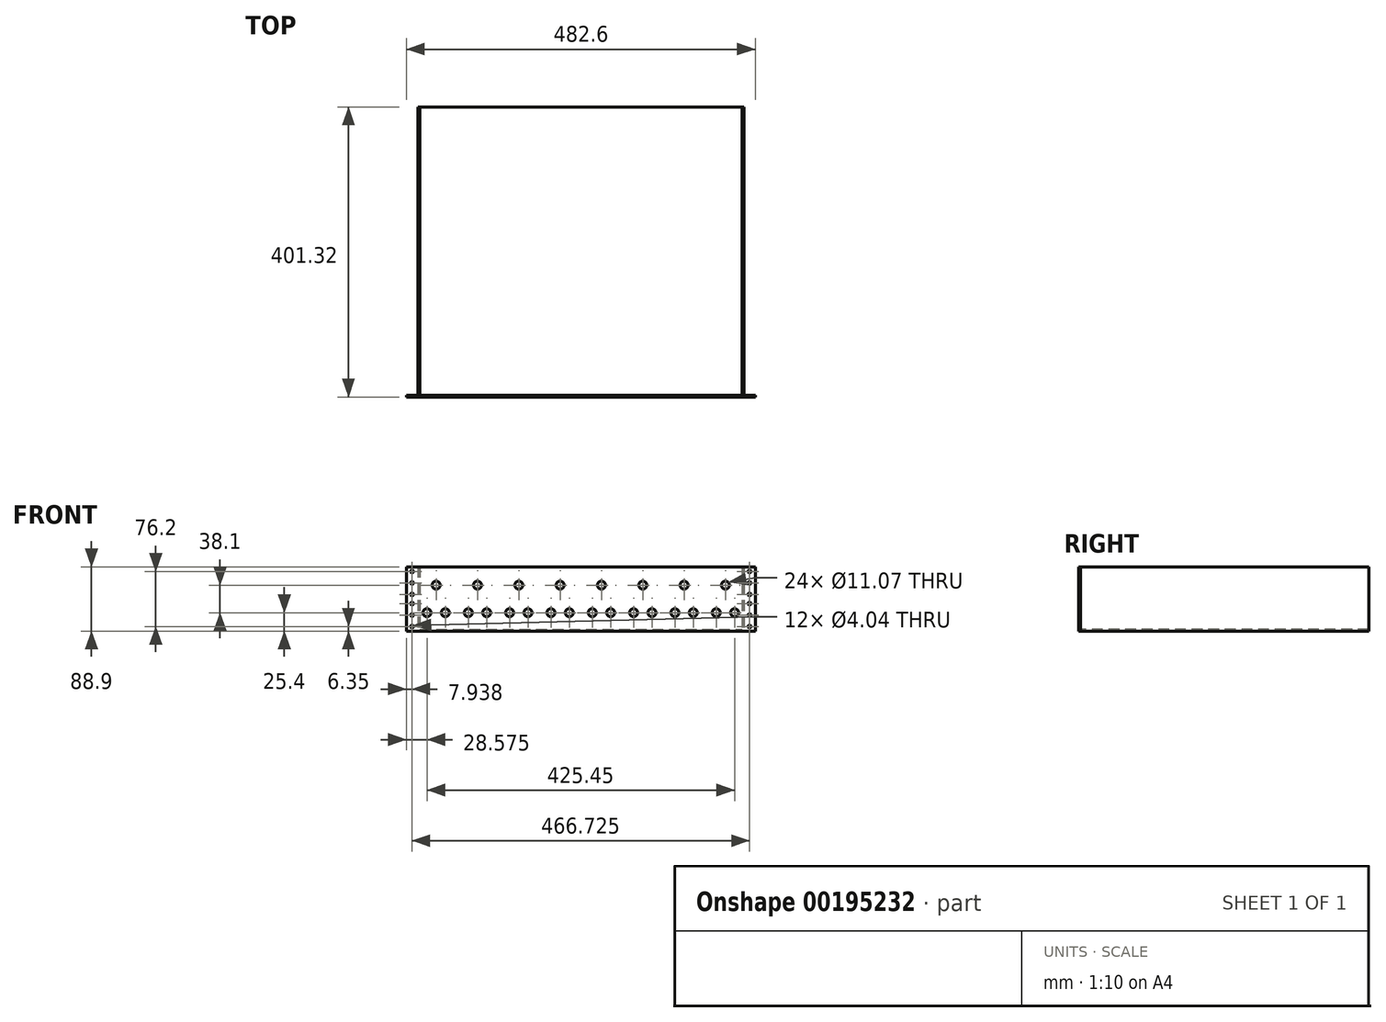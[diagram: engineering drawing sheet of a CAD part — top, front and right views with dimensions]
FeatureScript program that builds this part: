
annotation { "Feature Type Name" : "Feature", "Feature Type Description" : "" }
export const myFeature = defineFeature(function(context is Context, id is Id, definition is map)
    precondition{}
    {
        {
            var Q0;
            Q0=qCreatedBy(makeId("Front.planeOp"),FACE);
            var sketch = newSketch(context, id + "F0", { "sketchPlane" : qUnion([Q0])});
            skLineSegment(sketch, "E0.bottom", {"start": v(-241.3, 44.45) * mm, "end": v(241.3, 44.45) * mm});
            skLineSegment(sketch, "E0.top", {"start": v(-241.3, -44.45) * mm, "end": v(241.3, -44.45) * mm});
            skLineSegment(sketch, "E0.left", {"start": v(-241.3, 44.45) * mm, "end": v(-241.3, -44.45) * mm});
            skLineSegment(sketch, "E0.right", {"start": v(241.3, 44.45) * mm, "end": v(241.3, -44.45) * mm});
            skPoint(sketch, "E0.middle", {"position": v(0, 0) * mm});
            skCircle(sketch, "E1", {"center": v(-200.03, 19.05) * mm, "radius": 5.54 * mm});
            skCircle(sketch, "E2", {"center": v(-212.72, -19.05) * mm, "radius": 5.54 * mm});
            skCircle(sketch, "E3", {"center": v(-187.32, -19.05) * mm, "radius": 5.54 * mm});
            skCircle(sketch, "E4.1.0.0", {"center": v(-142.88, 19.05) * mm, "radius": 5.54 * mm});
            skCircle(sketch, "E4.1.0.1", {"center": v(-130.17, -19.05) * mm, "radius": 5.54 * mm});
            skCircle(sketch, "E4.1.0.2", {"center": v(-155.57, -19.05) * mm, "radius": 5.54 * mm});
            skCircle(sketch, "E4.2.0.0", {"center": v(-85.73, 19.05) * mm, "radius": 5.54 * mm});
            skCircle(sketch, "E4.2.0.1", {"center": v(-73.02, -19.05) * mm, "radius": 5.54 * mm});
            skCircle(sketch, "E4.2.0.2", {"center": v(-98.42, -19.05) * mm, "radius": 5.54 * mm});
            skCircle(sketch, "E4.3.0.0", {"center": v(-28.58, 19.05) * mm, "radius": 5.54 * mm});
            skCircle(sketch, "E4.3.0.1", {"center": v(-15.88, -19.05) * mm, "radius": 5.54 * mm});
            skCircle(sketch, "E4.3.0.2", {"center": v(-41.28, -19.05) * mm, "radius": 5.54 * mm});
            skCircle(sketch, "E4.4.0.0", {"center": v(28.57, 19.05) * mm, "radius": 5.54 * mm});
            skCircle(sketch, "E4.4.0.1", {"center": v(41.28, -19.05) * mm, "radius": 5.54 * mm});
            skCircle(sketch, "E4.4.0.2", {"center": v(15.88, -19.05) * mm, "radius": 5.54 * mm});
            skCircle(sketch, "E4.5.0.0", {"center": v(85.72, 19.05) * mm, "radius": 5.54 * mm});
            skCircle(sketch, "E4.5.0.1", {"center": v(98.43, -19.05) * mm, "radius": 5.54 * mm});
            skCircle(sketch, "E4.5.0.2", {"center": v(73.03, -19.05) * mm, "radius": 5.54 * mm});
            skCircle(sketch, "E4.6.0.0", {"center": v(142.87, 19.05) * mm, "radius": 5.54 * mm});
            skCircle(sketch, "E4.6.0.1", {"center": v(155.57, -19.05) * mm, "radius": 5.54 * mm});
            skCircle(sketch, "E4.6.0.2", {"center": v(130.17, -19.05) * mm, "radius": 5.54 * mm});
            skCircle(sketch, "E4.7.0.0", {"center": v(200.03, 19.05) * mm, "radius": 5.54 * mm});
            skCircle(sketch, "E4.7.0.1", {"center": v(212.73, -19.05) * mm, "radius": 5.54 * mm});
            skCircle(sketch, "E4.7.0.2", {"center": v(187.33, -19.05) * mm, "radius": 5.54 * mm});
            skLineSegment(sketch, "E4.direction1", {"start": v(-200.03, 19.05) * mm, "end": v(-142.88, 19.05) * mm, "construction": true});
            skSolve(sketch);
        }
        {
            var Q0;
            Q0=makeQuery(id+"F0.imprint","IMPRINT",FACE,{"disambiguationData":[TD([[makeQuery(id+"F0.imprint","IMPRINT",EDGE,{"derivedFrom":sQuery(id+"F0.wireOp",EDGE,"E0.bottom")}),-1.0]])]});
            extrude(context, id + "F1", {"entities" : qUnion([Q0]), "depth" : 2.54 * mm});
        }
        {
            var Q0;
            Q0=makeQuery(id+"F1.opExtrude","CAP_FACE",FACE,{"disambiguationData":[OSD([sQuery(id+"F0.wireOp",EDGE,"E0.bottom"),sQuery(id+"F0.wireOp",EDGE,"E0.top"),sQuery(id+"F0.wireOp",EDGE,"E0.left"),sQuery(id+"F0.wireOp",EDGE,"E0.right"),sQuery(id+"F0.wireOp",EDGE,"E1"),sQuery(id+"F0.wireOp",EDGE,"E2"),sQuery(id+"F0.wireOp",EDGE,"E3"),sQuery(id+"F0.wireOp",EDGE,"E4.1.0.0"),sQuery(id+"F0.wireOp",EDGE,"E4.1.0.1"),sQuery(id+"F0.wireOp",EDGE,"E4.1.0.2"),sQuery(id+"F0.wireOp",EDGE,"E4.2.0.0"),sQuery(id+"F0.wireOp",EDGE,"E4.2.0.1"),sQuery(id+"F0.wireOp",EDGE,"E4.2.0.2"),sQuery(id+"F0.wireOp",EDGE,"E4.3.0.0"),sQuery(id+"F0.wireOp",EDGE,"E4.3.0.1"),sQuery(id+"F0.wireOp",EDGE,"E4.3.0.2"),sQuery(id+"F0.wireOp",EDGE,"E4.4.0.0"),sQuery(id+"F0.wireOp",EDGE,"E4.4.0.1"),sQuery(id+"F0.wireOp",EDGE,"E4.4.0.2"),sQuery(id+"F0.wireOp",EDGE,"E4.5.0.0"),sQuery(id+"F0.wireOp",EDGE,"E4.5.0.1"),sQuery(id+"F0.wireOp",EDGE,"E4.5.0.2"),sQuery(id+"F0.wireOp",EDGE,"E4.6.0.0"),sQuery(id+"F0.wireOp",EDGE,"E4.6.0.1"),sQuery(id+"F0.wireOp",EDGE,"E4.6.0.2"),sQuery(id+"F0.wireOp",EDGE,"E4.7.0.0"),sQuery(id+"F0.wireOp",EDGE,"E4.7.0.1"),sQuery(id+"F0.wireOp",EDGE,"E4.7.0.2")])],"isStart":true});
            var sketch = newSketch(context, id + "F2", { "sketchPlane" : qUnion([Q0])});
            skLineSegment(sketch, "E5.bottom", {"start": v(-225.43, 44.45) * mm, "end": v(225.43, 44.45) * mm});
            skLineSegment(sketch, "E5.top", {"start": v(-225.43, -44.45) * mm, "end": v(225.43, -44.45) * mm});
            skLineSegment(sketch, "E5.left", {"start": v(-225.43, 44.45) * mm, "end": v(-225.43, -44.45) * mm});
            skLineSegment(sketch, "E5.right", {"start": v(225.43, 44.45) * mm, "end": v(225.43, -44.45) * mm});
            skPoint(sketch, "E5.middle", {"position": v(0, 0) * mm});
            skSolve(sketch);
        }
        {
            var Q0;
            Q0 = qSketchRegion(id + "F2", true);
            var Q1;
            Q1=sQuery(id+"F2.wireOp",EDGE,"E5.left");
            var Q2;
            Q2=sQuery(id+"F2.wireOp",EDGE,"E5.bottom");
            var Q3;
            Q3=sQuery(id+"F2.wireOp",EDGE,"E5.top");
            var Q4;
            Q4=sQuery(id+"F2.wireOp",EDGE,"E5.right");
            extrude(context, id + "F3", {"entities" : qUnion([Q0]), "operationType" : NewBodyOperationType.ADD, "surfaceEntities" : qUnion([Q1, Q2, Q3, Q4]), "depth" : 398.78 * mm});
        }
        {
            var Q0;
            Q0=makeQuery(id+"F3.boolean.opBoolean","SPLIT",FACE,{"disambiguationData":[TD([makeQuery(id+"F1.opExtrude","SWEPT_FACE",FACE,{"disambiguationData":[OSD([sQuery(id+"F0.wireOp",EDGE,"E1")])]})])],"derivedFrom":makeQuery(id+"F3.opExtrude","CAP_FACE",FACE,{"disambiguationData":[OSD([sQuery(id+"F2.wireOp",EDGE,"E5.bottom"),sQuery(id+"F2.wireOp",EDGE,"E5.top"),sQuery(id+"F2.wireOp",EDGE,"E5.left"),sQuery(id+"F2.wireOp",EDGE,"E5.right")])],"isStart":true})});
            var Q1;
            Q1=makeQuery(id+"F3.boolean.opBoolean","SPLIT",FACE,{"disambiguationData":[TD([makeQuery(id+"F1.opExtrude","SWEPT_FACE",FACE,{"disambiguationData":[OSD([sQuery(id+"F0.wireOp",EDGE,"E2")])]})])],"derivedFrom":makeQuery(id+"F3.opExtrude","CAP_FACE",FACE,{"disambiguationData":[OSD([sQuery(id+"F2.wireOp",EDGE,"E5.bottom"),sQuery(id+"F2.wireOp",EDGE,"E5.top"),sQuery(id+"F2.wireOp",EDGE,"E5.left"),sQuery(id+"F2.wireOp",EDGE,"E5.right")])],"isStart":true})});
            var Q2;
            Q2=makeQuery(id+"F3.boolean.opBoolean","SPLIT",FACE,{"disambiguationData":[TD([makeQuery(id+"F1.opExtrude","SWEPT_FACE",FACE,{"disambiguationData":[OSD([sQuery(id+"F0.wireOp",EDGE,"E3")])]})])],"derivedFrom":makeQuery(id+"F3.opExtrude","CAP_FACE",FACE,{"disambiguationData":[OSD([sQuery(id+"F2.wireOp",EDGE,"E5.bottom"),sQuery(id+"F2.wireOp",EDGE,"E5.top"),sQuery(id+"F2.wireOp",EDGE,"E5.left"),sQuery(id+"F2.wireOp",EDGE,"E5.right")])],"isStart":true})});
            var Q3;
            Q3=makeQuery(id+"F3.boolean.opBoolean","SPLIT",FACE,{"disambiguationData":[TD([makeQuery(id+"F1.opExtrude","SWEPT_FACE",FACE,{"disambiguationData":[OSD([sQuery(id+"F0.wireOp",EDGE,"E4.1.0.0")])]})])],"derivedFrom":makeQuery(id+"F3.opExtrude","CAP_FACE",FACE,{"disambiguationData":[OSD([sQuery(id+"F2.wireOp",EDGE,"E5.bottom"),sQuery(id+"F2.wireOp",EDGE,"E5.top"),sQuery(id+"F2.wireOp",EDGE,"E5.left"),sQuery(id+"F2.wireOp",EDGE,"E5.right")])],"isStart":true})});
            var Q4;
            Q4=makeQuery(id+"F3.boolean.opBoolean","SPLIT",FACE,{"disambiguationData":[TD([makeQuery(id+"F1.opExtrude","SWEPT_FACE",FACE,{"disambiguationData":[OSD([sQuery(id+"F0.wireOp",EDGE,"E4.1.0.2")])]})])],"derivedFrom":makeQuery(id+"F3.opExtrude","CAP_FACE",FACE,{"disambiguationData":[OSD([sQuery(id+"F2.wireOp",EDGE,"E5.bottom"),sQuery(id+"F2.wireOp",EDGE,"E5.top"),sQuery(id+"F2.wireOp",EDGE,"E5.left"),sQuery(id+"F2.wireOp",EDGE,"E5.right")])],"isStart":true})});
            var Q5;
            Q5=makeQuery(id+"F3.boolean.opBoolean","SPLIT",FACE,{"disambiguationData":[TD([makeQuery(id+"F1.opExtrude","SWEPT_FACE",FACE,{"disambiguationData":[OSD([sQuery(id+"F0.wireOp",EDGE,"E4.1.0.1")])]})])],"derivedFrom":makeQuery(id+"F3.opExtrude","CAP_FACE",FACE,{"disambiguationData":[OSD([sQuery(id+"F2.wireOp",EDGE,"E5.bottom"),sQuery(id+"F2.wireOp",EDGE,"E5.top"),sQuery(id+"F2.wireOp",EDGE,"E5.left"),sQuery(id+"F2.wireOp",EDGE,"E5.right")])],"isStart":true})});
            var Q6;
            Q6=makeQuery(id+"F3.boolean.opBoolean","SPLIT",FACE,{"disambiguationData":[TD([makeQuery(id+"F1.opExtrude","SWEPT_FACE",FACE,{"disambiguationData":[OSD([sQuery(id+"F0.wireOp",EDGE,"E4.2.0.0")])]})])],"derivedFrom":makeQuery(id+"F3.opExtrude","CAP_FACE",FACE,{"disambiguationData":[OSD([sQuery(id+"F2.wireOp",EDGE,"E5.bottom"),sQuery(id+"F2.wireOp",EDGE,"E5.top"),sQuery(id+"F2.wireOp",EDGE,"E5.left"),sQuery(id+"F2.wireOp",EDGE,"E5.right")])],"isStart":true})});
            var Q7;
            Q7=makeQuery(id+"F3.boolean.opBoolean","SPLIT",FACE,{"disambiguationData":[TD([makeQuery(id+"F1.opExtrude","SWEPT_FACE",FACE,{"disambiguationData":[OSD([sQuery(id+"F0.wireOp",EDGE,"E4.2.0.2")])]})])],"derivedFrom":makeQuery(id+"F3.opExtrude","CAP_FACE",FACE,{"disambiguationData":[OSD([sQuery(id+"F2.wireOp",EDGE,"E5.bottom"),sQuery(id+"F2.wireOp",EDGE,"E5.top"),sQuery(id+"F2.wireOp",EDGE,"E5.left"),sQuery(id+"F2.wireOp",EDGE,"E5.right")])],"isStart":true})});
            var Q8;
            Q8=makeQuery(id+"F3.boolean.opBoolean","SPLIT",FACE,{"disambiguationData":[TD([makeQuery(id+"F1.opExtrude","SWEPT_FACE",FACE,{"disambiguationData":[OSD([sQuery(id+"F0.wireOp",EDGE,"E4.2.0.1")])]})])],"derivedFrom":makeQuery(id+"F3.opExtrude","CAP_FACE",FACE,{"disambiguationData":[OSD([sQuery(id+"F2.wireOp",EDGE,"E5.bottom"),sQuery(id+"F2.wireOp",EDGE,"E5.top"),sQuery(id+"F2.wireOp",EDGE,"E5.left"),sQuery(id+"F2.wireOp",EDGE,"E5.right")])],"isStart":true})});
            var Q9;
            Q9=makeQuery(id+"F3.boolean.opBoolean","SPLIT",FACE,{"disambiguationData":[TD([makeQuery(id+"F1.opExtrude","SWEPT_FACE",FACE,{"disambiguationData":[OSD([sQuery(id+"F0.wireOp",EDGE,"E4.3.0.2")])]})])],"derivedFrom":makeQuery(id+"F3.opExtrude","CAP_FACE",FACE,{"disambiguationData":[OSD([sQuery(id+"F2.wireOp",EDGE,"E5.bottom"),sQuery(id+"F2.wireOp",EDGE,"E5.top"),sQuery(id+"F2.wireOp",EDGE,"E5.left"),sQuery(id+"F2.wireOp",EDGE,"E5.right")])],"isStart":true})});
            var Q10;
            Q10=makeQuery(id+"F3.boolean.opBoolean","SPLIT",FACE,{"disambiguationData":[TD([makeQuery(id+"F1.opExtrude","SWEPT_FACE",FACE,{"disambiguationData":[OSD([sQuery(id+"F0.wireOp",EDGE,"E4.3.0.0")])]})])],"derivedFrom":makeQuery(id+"F3.opExtrude","CAP_FACE",FACE,{"disambiguationData":[OSD([sQuery(id+"F2.wireOp",EDGE,"E5.bottom"),sQuery(id+"F2.wireOp",EDGE,"E5.top"),sQuery(id+"F2.wireOp",EDGE,"E5.left"),sQuery(id+"F2.wireOp",EDGE,"E5.right")])],"isStart":true})});
            var Q11;
            Q11=makeQuery(id+"F3.boolean.opBoolean","SPLIT",FACE,{"disambiguationData":[TD([makeQuery(id+"F1.opExtrude","SWEPT_FACE",FACE,{"disambiguationData":[OSD([sQuery(id+"F0.wireOp",EDGE,"E4.3.0.1")])]})])],"derivedFrom":makeQuery(id+"F3.opExtrude","CAP_FACE",FACE,{"disambiguationData":[OSD([sQuery(id+"F2.wireOp",EDGE,"E5.bottom"),sQuery(id+"F2.wireOp",EDGE,"E5.top"),sQuery(id+"F2.wireOp",EDGE,"E5.left"),sQuery(id+"F2.wireOp",EDGE,"E5.right")])],"isStart":true})});
            var Q12;
            Q12=makeQuery(id+"F3.boolean.opBoolean","SPLIT",FACE,{"disambiguationData":[TD([makeQuery(id+"F1.opExtrude","SWEPT_FACE",FACE,{"disambiguationData":[OSD([sQuery(id+"F0.wireOp",EDGE,"E4.4.0.2")])]})])],"derivedFrom":makeQuery(id+"F3.opExtrude","CAP_FACE",FACE,{"disambiguationData":[OSD([sQuery(id+"F2.wireOp",EDGE,"E5.bottom"),sQuery(id+"F2.wireOp",EDGE,"E5.top"),sQuery(id+"F2.wireOp",EDGE,"E5.left"),sQuery(id+"F2.wireOp",EDGE,"E5.right")])],"isStart":true})});
            var Q13;
            Q13=makeQuery(id+"F3.boolean.opBoolean","SPLIT",FACE,{"disambiguationData":[TD([makeQuery(id+"F1.opExtrude","SWEPT_FACE",FACE,{"disambiguationData":[OSD([sQuery(id+"F0.wireOp",EDGE,"E4.4.0.0")])]})])],"derivedFrom":makeQuery(id+"F3.opExtrude","CAP_FACE",FACE,{"disambiguationData":[OSD([sQuery(id+"F2.wireOp",EDGE,"E5.bottom"),sQuery(id+"F2.wireOp",EDGE,"E5.top"),sQuery(id+"F2.wireOp",EDGE,"E5.left"),sQuery(id+"F2.wireOp",EDGE,"E5.right")])],"isStart":true})});
            var Q14;
            Q14=makeQuery(id+"F3.boolean.opBoolean","SPLIT",FACE,{"disambiguationData":[TD([makeQuery(id+"F1.opExtrude","SWEPT_FACE",FACE,{"disambiguationData":[OSD([sQuery(id+"F0.wireOp",EDGE,"E4.4.0.1")])]})])],"derivedFrom":makeQuery(id+"F3.opExtrude","CAP_FACE",FACE,{"disambiguationData":[OSD([sQuery(id+"F2.wireOp",EDGE,"E5.bottom"),sQuery(id+"F2.wireOp",EDGE,"E5.top"),sQuery(id+"F2.wireOp",EDGE,"E5.left"),sQuery(id+"F2.wireOp",EDGE,"E5.right")])],"isStart":true})});
            var Q15;
            Q15=makeQuery(id+"F3.boolean.opBoolean","SPLIT",FACE,{"disambiguationData":[TD([makeQuery(id+"F1.opExtrude","SWEPT_FACE",FACE,{"disambiguationData":[OSD([sQuery(id+"F0.wireOp",EDGE,"E4.5.0.2")])]})])],"derivedFrom":makeQuery(id+"F3.opExtrude","CAP_FACE",FACE,{"disambiguationData":[OSD([sQuery(id+"F2.wireOp",EDGE,"E5.bottom"),sQuery(id+"F2.wireOp",EDGE,"E5.top"),sQuery(id+"F2.wireOp",EDGE,"E5.left"),sQuery(id+"F2.wireOp",EDGE,"E5.right")])],"isStart":true})});
            var Q16;
            Q16=makeQuery(id+"F3.boolean.opBoolean","SPLIT",FACE,{"disambiguationData":[TD([makeQuery(id+"F1.opExtrude","SWEPT_FACE",FACE,{"disambiguationData":[OSD([sQuery(id+"F0.wireOp",EDGE,"E4.5.0.0")])]})])],"derivedFrom":makeQuery(id+"F3.opExtrude","CAP_FACE",FACE,{"disambiguationData":[OSD([sQuery(id+"F2.wireOp",EDGE,"E5.bottom"),sQuery(id+"F2.wireOp",EDGE,"E5.top"),sQuery(id+"F2.wireOp",EDGE,"E5.left"),sQuery(id+"F2.wireOp",EDGE,"E5.right")])],"isStart":true})});
            var Q17;
            Q17=makeQuery(id+"F3.boolean.opBoolean","SPLIT",FACE,{"disambiguationData":[TD([makeQuery(id+"F1.opExtrude","SWEPT_FACE",FACE,{"disambiguationData":[OSD([sQuery(id+"F0.wireOp",EDGE,"E4.5.0.1")])]})])],"derivedFrom":makeQuery(id+"F3.opExtrude","CAP_FACE",FACE,{"disambiguationData":[OSD([sQuery(id+"F2.wireOp",EDGE,"E5.bottom"),sQuery(id+"F2.wireOp",EDGE,"E5.top"),sQuery(id+"F2.wireOp",EDGE,"E5.left"),sQuery(id+"F2.wireOp",EDGE,"E5.right")])],"isStart":true})});
            var Q18;
            Q18=makeQuery(id+"F3.boolean.opBoolean","SPLIT",FACE,{"disambiguationData":[TD([makeQuery(id+"F1.opExtrude","SWEPT_FACE",FACE,{"disambiguationData":[OSD([sQuery(id+"F0.wireOp",EDGE,"E4.6.0.2")])]})])],"derivedFrom":makeQuery(id+"F3.opExtrude","CAP_FACE",FACE,{"disambiguationData":[OSD([sQuery(id+"F2.wireOp",EDGE,"E5.bottom"),sQuery(id+"F2.wireOp",EDGE,"E5.top"),sQuery(id+"F2.wireOp",EDGE,"E5.left"),sQuery(id+"F2.wireOp",EDGE,"E5.right")])],"isStart":true})});
            var Q19;
            Q19=makeQuery(id+"F3.boolean.opBoolean","SPLIT",FACE,{"disambiguationData":[TD([makeQuery(id+"F1.opExtrude","SWEPT_FACE",FACE,{"disambiguationData":[OSD([sQuery(id+"F0.wireOp",EDGE,"E4.6.0.0")])]})])],"derivedFrom":makeQuery(id+"F3.opExtrude","CAP_FACE",FACE,{"disambiguationData":[OSD([sQuery(id+"F2.wireOp",EDGE,"E5.bottom"),sQuery(id+"F2.wireOp",EDGE,"E5.top"),sQuery(id+"F2.wireOp",EDGE,"E5.left"),sQuery(id+"F2.wireOp",EDGE,"E5.right")])],"isStart":true})});
            var Q20;
            Q20=makeQuery(id+"F3.boolean.opBoolean","SPLIT",FACE,{"disambiguationData":[TD([makeQuery(id+"F1.opExtrude","SWEPT_FACE",FACE,{"disambiguationData":[OSD([sQuery(id+"F0.wireOp",EDGE,"E4.6.0.1")])]})])],"derivedFrom":makeQuery(id+"F3.opExtrude","CAP_FACE",FACE,{"disambiguationData":[OSD([sQuery(id+"F2.wireOp",EDGE,"E5.bottom"),sQuery(id+"F2.wireOp",EDGE,"E5.top"),sQuery(id+"F2.wireOp",EDGE,"E5.left"),sQuery(id+"F2.wireOp",EDGE,"E5.right")])],"isStart":true})});
            var Q21;
            Q21=makeQuery(id+"F3.boolean.opBoolean","SPLIT",FACE,{"disambiguationData":[TD([makeQuery(id+"F1.opExtrude","SWEPT_FACE",FACE,{"disambiguationData":[OSD([sQuery(id+"F0.wireOp",EDGE,"E4.7.0.2")])]})])],"derivedFrom":makeQuery(id+"F3.opExtrude","CAP_FACE",FACE,{"disambiguationData":[OSD([sQuery(id+"F2.wireOp",EDGE,"E5.bottom"),sQuery(id+"F2.wireOp",EDGE,"E5.top"),sQuery(id+"F2.wireOp",EDGE,"E5.left"),sQuery(id+"F2.wireOp",EDGE,"E5.right")])],"isStart":true})});
            var Q22;
            Q22=makeQuery(id+"F3.boolean.opBoolean","SPLIT",FACE,{"disambiguationData":[TD([makeQuery(id+"F1.opExtrude","SWEPT_FACE",FACE,{"disambiguationData":[OSD([sQuery(id+"F0.wireOp",EDGE,"E4.7.0.0")])]})])],"derivedFrom":makeQuery(id+"F3.opExtrude","CAP_FACE",FACE,{"disambiguationData":[OSD([sQuery(id+"F2.wireOp",EDGE,"E5.bottom"),sQuery(id+"F2.wireOp",EDGE,"E5.top"),sQuery(id+"F2.wireOp",EDGE,"E5.left"),sQuery(id+"F2.wireOp",EDGE,"E5.right")])],"isStart":true})});
            var Q23;
            Q23=makeQuery(id+"F3.boolean.opBoolean","SPLIT",FACE,{"disambiguationData":[TD([makeQuery(id+"F1.opExtrude","SWEPT_FACE",FACE,{"disambiguationData":[OSD([sQuery(id+"F0.wireOp",EDGE,"E4.7.0.1")])]})])],"derivedFrom":makeQuery(id+"F3.opExtrude","CAP_FACE",FACE,{"disambiguationData":[OSD([sQuery(id+"F2.wireOp",EDGE,"E5.bottom"),sQuery(id+"F2.wireOp",EDGE,"E5.top"),sQuery(id+"F2.wireOp",EDGE,"E5.left"),sQuery(id+"F2.wireOp",EDGE,"E5.right")])],"isStart":true})});
            extrude(context, id + "F4", {"entities" : qUnion([Q0, Q1, Q2, Q3, Q4, Q5, Q6, Q7, Q8, Q9, Q10, Q11, Q12, Q13, Q14, Q15, Q16, Q17, Q18, Q19, Q20, Q21, Q22, Q23]), "operationType" : NewBodyOperationType.REMOVE, "endBound" : BoundingType.THROUGH_ALL, "oppositeDirection" : true, "depth" : 25.4 * mm});
        }
        {
            var Q0;
            Q0=makeQuery(id+"F1.opExtrude","CAP_FACE",FACE,{"disambiguationData":[OSD([sQuery(id+"F0.wireOp",EDGE,"E0.bottom"),sQuery(id+"F0.wireOp",EDGE,"E0.top"),sQuery(id+"F0.wireOp",EDGE,"E0.left"),sQuery(id+"F0.wireOp",EDGE,"E0.right"),sQuery(id+"F0.wireOp",EDGE,"E1"),sQuery(id+"F0.wireOp",EDGE,"E2"),sQuery(id+"F0.wireOp",EDGE,"E3"),sQuery(id+"F0.wireOp",EDGE,"E4.1.0.0"),sQuery(id+"F0.wireOp",EDGE,"E4.1.0.1"),sQuery(id+"F0.wireOp",EDGE,"E4.1.0.2"),sQuery(id+"F0.wireOp",EDGE,"E4.2.0.0"),sQuery(id+"F0.wireOp",EDGE,"E4.2.0.1"),sQuery(id+"F0.wireOp",EDGE,"E4.2.0.2"),sQuery(id+"F0.wireOp",EDGE,"E4.3.0.0"),sQuery(id+"F0.wireOp",EDGE,"E4.3.0.1"),sQuery(id+"F0.wireOp",EDGE,"E4.3.0.2"),sQuery(id+"F0.wireOp",EDGE,"E4.4.0.0"),sQuery(id+"F0.wireOp",EDGE,"E4.4.0.1"),sQuery(id+"F0.wireOp",EDGE,"E4.4.0.2"),sQuery(id+"F0.wireOp",EDGE,"E4.5.0.0"),sQuery(id+"F0.wireOp",EDGE,"E4.5.0.1"),sQuery(id+"F0.wireOp",EDGE,"E4.5.0.2"),sQuery(id+"F0.wireOp",EDGE,"E4.6.0.0"),sQuery(id+"F0.wireOp",EDGE,"E4.6.0.1"),sQuery(id+"F0.wireOp",EDGE,"E4.6.0.2"),sQuery(id+"F0.wireOp",EDGE,"E4.7.0.0"),sQuery(id+"F0.wireOp",EDGE,"E4.7.0.1"),sQuery(id+"F0.wireOp",EDGE,"E4.7.0.2")])],"isStart":false});
            var sketch = newSketch(context, id + "F5", { "sketchPlane" : qUnion([Q0])});
            skPoint(sketch, "E6", {"position": v(-233.36, 38.1) * mm});
            skPoint(sketch, "E7", {"position": v(-233.36, 22.22) * mm});
            skPoint(sketch, "E8", {"position": v(-233.36, 6.35) * mm});
            skPoint(sketch, "E9.0.1.0", {"position": v(-233.36, -6.35) * mm});
            skPoint(sketch, "E9.0.1.1", {"position": v(-233.36, -22.23) * mm});
            skPoint(sketch, "E9.0.1.2", {"position": v(-233.36, -38.1) * mm});
            skPoint(sketch, "E9.1.0.0", {"position": v(233.36, 38.1) * mm});
            skPoint(sketch, "E9.1.0.1", {"position": v(233.36, 22.22) * mm});
            skPoint(sketch, "E9.1.0.2", {"position": v(233.36, 6.35) * mm});
            skPoint(sketch, "E9.1.1.0", {"position": v(233.36, -6.35) * mm});
            skPoint(sketch, "E9.1.1.1", {"position": v(233.36, -22.23) * mm});
            skPoint(sketch, "E9.1.1.2", {"position": v(233.36, -38.1) * mm});
            skLineSegment(sketch, "E9.direction1", {"start": v(-233.36, 38.1) * mm, "end": v(233.36, 38.1) * mm, "construction": true});
            skLineSegment(sketch, "E9.direction2", {"start": v(-233.36, 38.1) * mm, "end": v(-233.36, -6.35) * mm, "construction": true});
            skSolve(sketch);
        }
        {
            var Q0;
            Q0=sQuery(id+"F5.wireOp",VERTEX,"E9.1.1.2");
            var Q1;
            Q1=sQuery(id+"F5.wireOp",VERTEX,"E9.1.1.0");
            var Q2;
            Q2=sQuery(id+"F5.wireOp",VERTEX,"E7");
            var Q3;
            Q3=sQuery(id+"F5.wireOp",VERTEX,"E9.1.1.1");
            var Q4;
            Q4=sQuery(id+"F5.wireOp",VERTEX,"E6");
            var Q5;
            Q5=sQuery(id+"F5.wireOp",VERTEX,"E8");
            var Q6;
            Q6=sQuery(id+"F5.wireOp",VERTEX,"E9.0.1.1");
            var Q7;
            Q7=sQuery(id+"F5.wireOp",VERTEX,"E9.0.1.0");
            var Q8;
            Q8=sQuery(id+"F5.wireOp",VERTEX,"E9.0.1.2");
            var Q9;
            Q9=sQuery(id+"F5.wireOp",VERTEX,"E9.1.0.0");
            var Q10;
            Q10=sQuery(id+"F5.wireOp",VERTEX,"E9.1.0.1");
            var Q11;
            Q11=sQuery(id+"F5.wireOp",VERTEX,"E9.1.0.2");
            var Q12;
            Q12=makeQuery(id+"F1.opExtrude","SWEPT_BODY",BODY,{"disambiguationData":[OSD([sQuery(id+"F0.wireOp",EDGE,"E0.bottom"),sQuery(id+"F0.wireOp",EDGE,"E0.top"),sQuery(id+"F0.wireOp",EDGE,"E0.left"),sQuery(id+"F0.wireOp",EDGE,"E0.right"),sQuery(id+"F0.wireOp",EDGE,"E1"),sQuery(id+"F0.wireOp",EDGE,"E2"),sQuery(id+"F0.wireOp",EDGE,"E3"),sQuery(id+"F0.wireOp",EDGE,"E4.1.0.0"),sQuery(id+"F0.wireOp",EDGE,"E4.1.0.1"),sQuery(id+"F0.wireOp",EDGE,"E4.1.0.2"),sQuery(id+"F0.wireOp",EDGE,"E4.2.0.0"),sQuery(id+"F0.wireOp",EDGE,"E4.2.0.1"),sQuery(id+"F0.wireOp",EDGE,"E4.2.0.2"),sQuery(id+"F0.wireOp",EDGE,"E4.3.0.0"),sQuery(id+"F0.wireOp",EDGE,"E4.3.0.1"),sQuery(id+"F0.wireOp",EDGE,"E4.3.0.2"),sQuery(id+"F0.wireOp",EDGE,"E4.4.0.0"),sQuery(id+"F0.wireOp",EDGE,"E4.4.0.1"),sQuery(id+"F0.wireOp",EDGE,"E4.4.0.2"),sQuery(id+"F0.wireOp",EDGE,"E4.5.0.0"),sQuery(id+"F0.wireOp",EDGE,"E4.5.0.1"),sQuery(id+"F0.wireOp",EDGE,"E4.5.0.2"),sQuery(id+"F0.wireOp",EDGE,"E4.6.0.0"),sQuery(id+"F0.wireOp",EDGE,"E4.6.0.1"),sQuery(id+"F0.wireOp",EDGE,"E4.6.0.2"),sQuery(id+"F0.wireOp",EDGE,"E4.7.0.0"),sQuery(id+"F0.wireOp",EDGE,"E4.7.0.1"),sQuery(id+"F0.wireOp",EDGE,"E4.7.0.2")])]});
            hole(context, id + "F6", {"style" : HoleStyle.SIMPLE, "endStyle" : HoleEndStyle.THROUGH, "standardTappedOrClearance" : lookupTablePath({ "standard" : "ANSI", "engagement" : "75%", "pitch" : "32 tpi", "size" : "#10", "type" : "Tapped" }), "standardBlindInLast" : lookupTablePath({ "standard" : "ANSI", "engagement" : "75%", "pitch" : "32 tpi", "size" : "#10", "type" : "Tapped" }), "holeDiameter" : 4.04 * mm, "locations" : qUnion([Q0, Q1, Q2, Q3, Q4, Q5, Q6, Q7, Q8, Q9, Q10, Q11]), "scope" : qUnion([Q12]), "isTappedThrough" : true, "majorDiameter" : 4.83 * mm, "showTappedDepth" : true});
        }
        {
            var Q0;
            {var subQ0=sQuery(id+"F0.wireOp",EDGE,"E4.4.0.0");Q0=makeQuery(id+"F4.boolean.opBoolean","MERGE",FACE,{"derivedFrom":[makeQuery(id+"F1.opExtrude","SWEPT_FACE",FACE,{"disambiguationData":[OSD([subQ0])]}),makeQuery(id+"F4.opExtrude","SWEPT_FACE",FACE,{"disambiguationData":[OSD([subQ0])]})]});}
            var Q1;
            {var subQ0=sQuery(id+"F0.wireOp",EDGE,"E4.2.0.2");Q1=makeQuery(id+"F4.boolean.opBoolean","MERGE",FACE,{"derivedFrom":[makeQuery(id+"F1.opExtrude","SWEPT_FACE",FACE,{"disambiguationData":[OSD([subQ0])]}),makeQuery(id+"F4.opExtrude","SWEPT_FACE",FACE,{"disambiguationData":[OSD([subQ0])]})]});}
            var Q2;
            {var subQ0=sQuery(id+"F0.wireOp",EDGE,"E4.1.0.1");Q2=makeQuery(id+"F4.boolean.opBoolean","MERGE",FACE,{"derivedFrom":[makeQuery(id+"F1.opExtrude","SWEPT_FACE",FACE,{"disambiguationData":[OSD([subQ0])]}),makeQuery(id+"F4.opExtrude","SWEPT_FACE",FACE,{"disambiguationData":[OSD([subQ0])]})]});}
            var Q3;
            {var subQ0=sQuery(id+"F0.wireOp",EDGE,"E4.1.0.2");Q3=makeQuery(id+"F4.boolean.opBoolean","MERGE",FACE,{"derivedFrom":[makeQuery(id+"F1.opExtrude","SWEPT_FACE",FACE,{"disambiguationData":[OSD([subQ0])]}),makeQuery(id+"F4.opExtrude","SWEPT_FACE",FACE,{"disambiguationData":[OSD([subQ0])]})]});}
            var Q4;
            {var subQ0=sQuery(id+"F0.wireOp",EDGE,"E3");Q4=makeQuery(id+"F4.boolean.opBoolean","MERGE",FACE,{"derivedFrom":[makeQuery(id+"F1.opExtrude","SWEPT_FACE",FACE,{"disambiguationData":[OSD([subQ0])]}),makeQuery(id+"F4.opExtrude","SWEPT_FACE",FACE,{"disambiguationData":[OSD([subQ0])]})]});}
            var Q5;
            {var subQ0=sQuery(id+"F0.wireOp",EDGE,"E2");Q5=makeQuery(id+"F4.boolean.opBoolean","MERGE",FACE,{"derivedFrom":[makeQuery(id+"F1.opExtrude","SWEPT_FACE",FACE,{"disambiguationData":[OSD([subQ0])]}),makeQuery(id+"F4.opExtrude","SWEPT_FACE",FACE,{"disambiguationData":[OSD([subQ0])]})]});}
            var Q6;
            {var subQ0=sQuery(id+"F0.wireOp",EDGE,"E1");Q6=makeQuery(id+"F4.boolean.opBoolean","MERGE",FACE,{"derivedFrom":[makeQuery(id+"F1.opExtrude","SWEPT_FACE",FACE,{"disambiguationData":[OSD([subQ0])]}),makeQuery(id+"F4.opExtrude","SWEPT_FACE",FACE,{"disambiguationData":[OSD([subQ0])]})]});}
            var Q7;
            {var subQ0=sQuery(id+"F0.wireOp",EDGE,"E4.1.0.0");Q7=makeQuery(id+"F4.boolean.opBoolean","MERGE",FACE,{"derivedFrom":[makeQuery(id+"F1.opExtrude","SWEPT_FACE",FACE,{"disambiguationData":[OSD([subQ0])]}),makeQuery(id+"F4.opExtrude","SWEPT_FACE",FACE,{"disambiguationData":[OSD([subQ0])]})]});}
            var Q8;
            {var subQ0=sQuery(id+"F0.wireOp",EDGE,"E4.2.0.0");Q8=makeQuery(id+"F4.boolean.opBoolean","MERGE",FACE,{"derivedFrom":[makeQuery(id+"F1.opExtrude","SWEPT_FACE",FACE,{"disambiguationData":[OSD([subQ0])]}),makeQuery(id+"F4.opExtrude","SWEPT_FACE",FACE,{"disambiguationData":[OSD([subQ0])]})]});}
            var Q9;
            {var subQ0=sQuery(id+"F0.wireOp",EDGE,"E4.2.0.1");Q9=makeQuery(id+"F4.boolean.opBoolean","MERGE",FACE,{"derivedFrom":[makeQuery(id+"F1.opExtrude","SWEPT_FACE",FACE,{"disambiguationData":[OSD([subQ0])]}),makeQuery(id+"F4.opExtrude","SWEPT_FACE",FACE,{"disambiguationData":[OSD([subQ0])]})]});}
            var Q10;
            {var subQ0=sQuery(id+"F0.wireOp",EDGE,"E4.3.0.0");Q10=makeQuery(id+"F4.boolean.opBoolean","MERGE",FACE,{"derivedFrom":[makeQuery(id+"F1.opExtrude","SWEPT_FACE",FACE,{"disambiguationData":[OSD([subQ0])]}),makeQuery(id+"F4.opExtrude","SWEPT_FACE",FACE,{"disambiguationData":[OSD([subQ0])]})]});}
            var Q11;
            {var subQ0=sQuery(id+"F0.wireOp",EDGE,"E4.3.0.2");Q11=makeQuery(id+"F4.boolean.opBoolean","MERGE",FACE,{"derivedFrom":[makeQuery(id+"F1.opExtrude","SWEPT_FACE",FACE,{"disambiguationData":[OSD([subQ0])]}),makeQuery(id+"F4.opExtrude","SWEPT_FACE",FACE,{"disambiguationData":[OSD([subQ0])]})]});}
            var Q12;
            {var subQ0=sQuery(id+"F0.wireOp",EDGE,"E4.3.0.1");Q12=makeQuery(id+"F4.boolean.opBoolean","MERGE",FACE,{"derivedFrom":[makeQuery(id+"F1.opExtrude","SWEPT_FACE",FACE,{"disambiguationData":[OSD([subQ0])]}),makeQuery(id+"F4.opExtrude","SWEPT_FACE",FACE,{"disambiguationData":[OSD([subQ0])]})]});}
            var Q13;
            {var subQ0=sQuery(id+"F0.wireOp",EDGE,"E4.4.0.2");Q13=makeQuery(id+"F4.boolean.opBoolean","MERGE",FACE,{"derivedFrom":[makeQuery(id+"F1.opExtrude","SWEPT_FACE",FACE,{"disambiguationData":[OSD([subQ0])]}),makeQuery(id+"F4.opExtrude","SWEPT_FACE",FACE,{"disambiguationData":[OSD([subQ0])]})]});}
            var Q14;
            {var subQ0=sQuery(id+"F0.wireOp",EDGE,"E4.4.0.1");Q14=makeQuery(id+"F4.boolean.opBoolean","MERGE",FACE,{"derivedFrom":[makeQuery(id+"F1.opExtrude","SWEPT_FACE",FACE,{"disambiguationData":[OSD([subQ0])]}),makeQuery(id+"F4.opExtrude","SWEPT_FACE",FACE,{"disambiguationData":[OSD([subQ0])]})]});}
            var Q15;
            {var subQ0=sQuery(id+"F0.wireOp",EDGE,"E4.5.0.2");Q15=makeQuery(id+"F4.boolean.opBoolean","MERGE",FACE,{"derivedFrom":[makeQuery(id+"F1.opExtrude","SWEPT_FACE",FACE,{"disambiguationData":[OSD([subQ0])]}),makeQuery(id+"F4.opExtrude","SWEPT_FACE",FACE,{"disambiguationData":[OSD([subQ0])]})]});}
            var Q16;
            {var subQ0=sQuery(id+"F0.wireOp",EDGE,"E4.5.0.0");Q16=makeQuery(id+"F4.boolean.opBoolean","MERGE",FACE,{"derivedFrom":[makeQuery(id+"F1.opExtrude","SWEPT_FACE",FACE,{"disambiguationData":[OSD([subQ0])]}),makeQuery(id+"F4.opExtrude","SWEPT_FACE",FACE,{"disambiguationData":[OSD([subQ0])]})]});}
            var Q17;
            {var subQ0=sQuery(id+"F0.wireOp",EDGE,"E4.5.0.1");Q17=makeQuery(id+"F4.boolean.opBoolean","MERGE",FACE,{"derivedFrom":[makeQuery(id+"F1.opExtrude","SWEPT_FACE",FACE,{"disambiguationData":[OSD([subQ0])]}),makeQuery(id+"F4.opExtrude","SWEPT_FACE",FACE,{"disambiguationData":[OSD([subQ0])]})]});}
            var Q18;
            {var subQ0=sQuery(id+"F0.wireOp",EDGE,"E4.6.0.2");Q18=makeQuery(id+"F4.boolean.opBoolean","MERGE",FACE,{"derivedFrom":[makeQuery(id+"F1.opExtrude","SWEPT_FACE",FACE,{"disambiguationData":[OSD([subQ0])]}),makeQuery(id+"F4.opExtrude","SWEPT_FACE",FACE,{"disambiguationData":[OSD([subQ0])]})]});}
            var Q19;
            {var subQ0=sQuery(id+"F0.wireOp",EDGE,"E4.6.0.1");Q19=makeQuery(id+"F4.boolean.opBoolean","MERGE",FACE,{"derivedFrom":[makeQuery(id+"F1.opExtrude","SWEPT_FACE",FACE,{"disambiguationData":[OSD([subQ0])]}),makeQuery(id+"F4.opExtrude","SWEPT_FACE",FACE,{"disambiguationData":[OSD([subQ0])]})]});}
            var Q20;
            {var subQ0=sQuery(id+"F0.wireOp",EDGE,"E4.7.0.2");Q20=makeQuery(id+"F4.boolean.opBoolean","MERGE",FACE,{"derivedFrom":[makeQuery(id+"F1.opExtrude","SWEPT_FACE",FACE,{"disambiguationData":[OSD([subQ0])]}),makeQuery(id+"F4.opExtrude","SWEPT_FACE",FACE,{"disambiguationData":[OSD([subQ0])]})]});}
            var Q21;
            {var subQ0=sQuery(id+"F0.wireOp",EDGE,"E4.7.0.1");Q21=makeQuery(id+"F4.boolean.opBoolean","MERGE",FACE,{"derivedFrom":[makeQuery(id+"F1.opExtrude","SWEPT_FACE",FACE,{"disambiguationData":[OSD([subQ0])]}),makeQuery(id+"F4.opExtrude","SWEPT_FACE",FACE,{"disambiguationData":[OSD([subQ0])]})]});}
            var Q22;
            {var subQ0=sQuery(id+"F0.wireOp",EDGE,"E4.7.0.0");Q22=makeQuery(id+"F4.boolean.opBoolean","MERGE",FACE,{"derivedFrom":[makeQuery(id+"F1.opExtrude","SWEPT_FACE",FACE,{"disambiguationData":[OSD([subQ0])]}),makeQuery(id+"F4.opExtrude","SWEPT_FACE",FACE,{"disambiguationData":[OSD([subQ0])]})]});}
            var Q23;
            {var subQ0=sQuery(id+"F0.wireOp",EDGE,"E4.6.0.0");Q23=makeQuery(id+"F4.boolean.opBoolean","MERGE",FACE,{"derivedFrom":[makeQuery(id+"F1.opExtrude","SWEPT_FACE",FACE,{"disambiguationData":[OSD([subQ0])]}),makeQuery(id+"F4.opExtrude","SWEPT_FACE",FACE,{"disambiguationData":[OSD([subQ0])]})]});}
            var Q24;
            Q24=makeQuery(id+"F3.boolean.opBoolean","MERGE",FACE,{"derivedFrom":[makeQuery(id+"F1.opExtrude","SWEPT_FACE",FACE,{"disambiguationData":[OSD([sQuery(id+"F0.wireOp",EDGE,"E0.bottom")])]}),makeQuery(id+"F3.opExtrude","SWEPT_FACE",FACE,{"disambiguationData":[OSD([sQuery(id+"F2.wireOp",EDGE,"E5.bottom")])]})]});
            var Q25;
            Q25=makeQuery(id+"F3.opExtrude","CAP_FACE",FACE,{"disambiguationData":[OSD([sQuery(id+"F2.wireOp",EDGE,"E5.bottom"),sQuery(id+"F2.wireOp",EDGE,"E5.top"),sQuery(id+"F2.wireOp",EDGE,"E5.left"),sQuery(id+"F2.wireOp",EDGE,"E5.right")])],"isStart":false});
            shell(context, id + "F7", {"entities" : qUnion([Q0, Q1, Q2, Q3, Q4, Q5, Q6, Q7, Q8, Q9, Q10, Q11, Q12, Q13, Q14, Q15, Q16, Q17, Q18, Q19, Q20, Q21, Q22, Q23, Q24, Q25]), "thickness" : 2.54 * mm});
        }
    });
